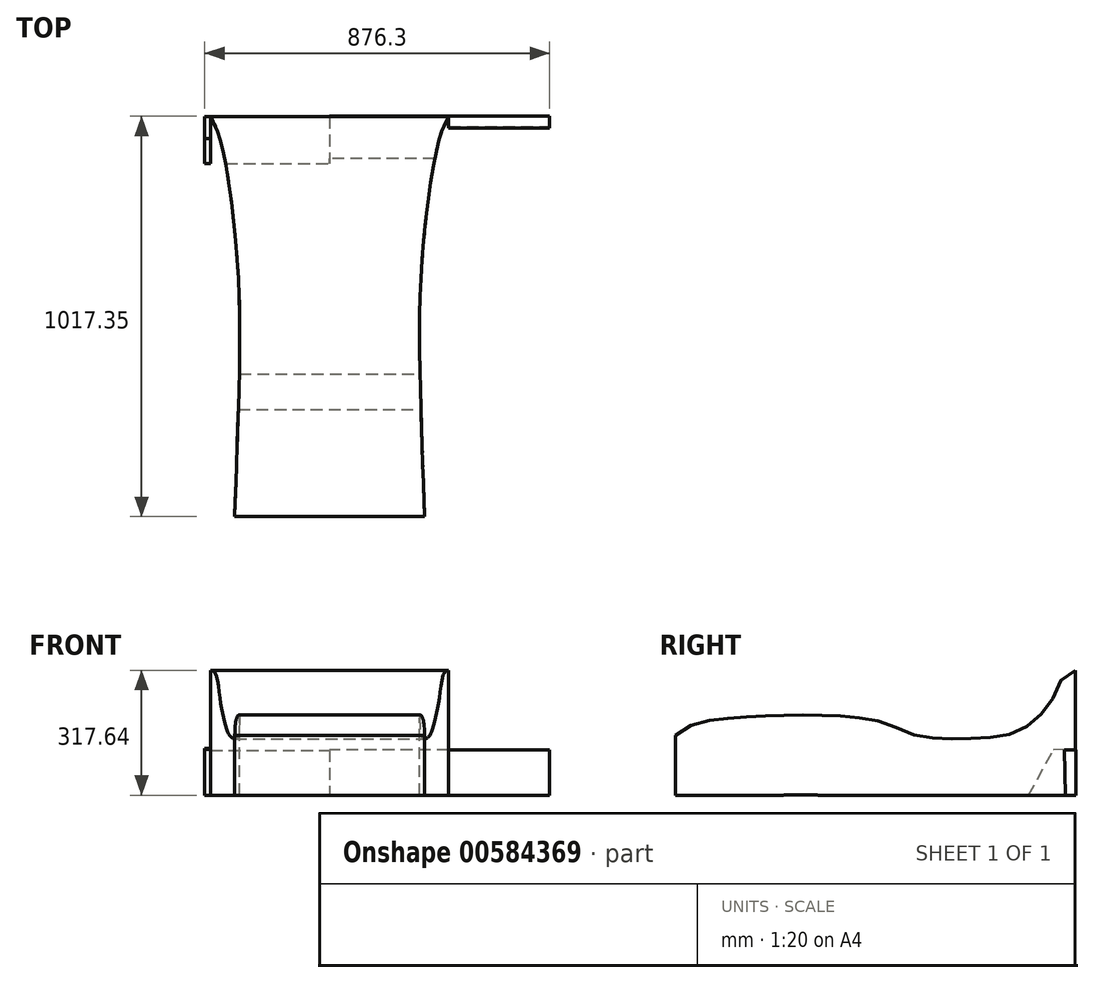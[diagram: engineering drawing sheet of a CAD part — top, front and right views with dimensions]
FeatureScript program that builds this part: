
annotation { "Feature Type Name" : "Feature", "Feature Type Description" : "" }
export const myFeature = defineFeature(function(context is Context, id is Id, definition is map)
    precondition{}
    {
        {
            var Q0;
            Q0=qCreatedBy(makeId("Front.planeOp"),FACE);
            var sketch = newSketch(context, id + "F0", { "sketchPlane" : qUnion([Q0])});
            skLineSegment(sketch, "E0", {"start": v(0, 0) * mm, "end": v(241.3, 0) * mm});
            skLineSegment(sketch, "E1", {"start": v(241.3, 0) * mm, "end": v(241.3, -38.1) * mm});
            skLineSegment(sketch, "E2", {"start": v(241.3, -38.1) * mm, "end": v(0, -38.1) * mm});
            skLineSegment(sketch, "E3", {"start": v(0, -38.1) * mm, "end": v(-241.3, -38.1) * mm});
            skLineSegment(sketch, "E4", {"start": v(-241.3, -38.1) * mm, "end": v(-241.3, 0) * mm});
            skLineSegment(sketch, "E5", {"start": v(-241.3, 0) * mm, "end": v(0, 0) * mm});
            skSolve(sketch);
        }
        {
            var Q0;
            Q0=qCreatedBy(makeId("Right.planeOp"),FACE);
            var sketch = newSketch(context, id + "F1", { "sketchPlane" : qUnion([Q0])});
            skFitSpline(sketch, "E6", {"points": [v(0, 0) * mm, v(24.74, 16.6) * mm, v(49, 28.94) * mm, v(187.46, 47.43) * mm, v(521.37, 34.71) * mm, v(607.94, 0) * mm, v(838.07, 0) * mm, v(901.63, 29.24) * mm, v(960.8, 98.27) * mm, v(1016, 165.1) * mm], "startDerivative": vector(273.3, 180.11) * mm, "endDerivative": vector(1078.66, 86.3) * mm});
            skLineSegment(sketch, "E7.0", {"start": v(0, -38.1) * mm, "end": v(0, 0) * mm, "construction": true});
            skLineSegment(sketch, "E8", {"start": v(0, -38.1) * mm, "end": v(1016, -38.1) * mm});
            skLineSegment(sketch, "E9", {"start": v(1016, 165.1) * mm, "end": v(1016, -38.1) * mm, "construction": true});
            skSolve(sketch);
        }
        {
            var Q0;
            Q0=qCreatedBy(makeId("Front.planeOp"),FACE);
            cPlane(context, id + "F2", {"entities" : qUnion([Q0]), "cplaneType" : CPlaneType.OFFSET, "offset" : 1016 * mm, "oppositeDirection" : true, "width" : 152.4 * mm, "height" : 152.4 * mm});
        }
        {
            var Q0;
            Q0=qCreatedBy(id+"F2.planeOp",FACE);
            var sketch = newSketch(context, id + "F3", { "sketchPlane" : qUnion([Q0])});
            skPoint(sketch, "E10.0", {"position": v(0, 165.1) * mm});
            skPoint(sketch, "E11.0", {"position": v(0, -38.1) * mm});
            skLineSegment(sketch, "E12", {"start": v(0, 165.1) * mm, "end": v(302.62, 165.1) * mm});
            skLineSegment(sketch, "E13", {"start": v(302.62, 165.1) * mm, "end": v(302.62, -38.1) * mm});
            skLineSegment(sketch, "E14", {"start": v(302.62, -38.1) * mm, "end": v(0, -38.1) * mm});
            skLineSegment(sketch, "E15", {"start": v(0, 165.1) * mm, "end": v(0, -38.1) * mm, "construction": true});
            skLineSegment(sketch, "E16.MirrorCS", {"start": v(0, 165.1) * mm, "end": v(-302.62, 165.1) * mm});
            skLineSegment(sketch, "E17.MirrorCS", {"start": v(-302.62, 165.1) * mm, "end": v(-302.62, -38.1) * mm});
            skLineSegment(sketch, "E18.MirrorCS", {"start": v(-302.62, -38.1) * mm, "end": v(0, -38.1) * mm});
            skSolve(sketch);
        }
        {
            var Q0;
            Q0=makeQuery(id+"F3.imprint","IMPRINT",FACE,{"disambiguationData":[TD([[makeQuery(id+"F3.imprint","IMPRINT",EDGE,{"derivedFrom":sQuery(id+"F3.wireOp",EDGE,"E12")}),-1.0]])]});
            var Q1;
            Q1=sQuery(id+"F1.wireOp",EDGE,"E6");
            sweep(context, id + "F4", {"profiles" : qUnion([Q0]), "path" : qUnion([Q1]), "keepProfileOrientation" : true});
        }
        {
            var Q0;
            Q0=qCreatedBy(makeId("Right.planeOp"),FACE);
            var sketch = newSketch(context, id + "F5", { "sketchPlane" : qUnion([Q0])});
            skLineSegment(sketch, "E19", {"start": v(0, -254) * mm, "end": v(1016, -254) * mm});
            skLineSegment(sketch, "E20", {"start": v(0, -254) * mm, "end": v(0, 0) * mm, "construction": true});
            skLineSegment(sketch, "E21", {"start": v(0, 0) * mm, "end": v(4.95, -3.69) * mm});
            skLineSegment(sketch, "E22", {"start": v(0, -254) * mm, "end": v(0, -152.4) * mm});
            skLineSegment(sketch, "E23", {"start": v(0, -152.4) * mm, "end": v(1016, -152.4) * mm});
            skLineSegment(sketch, "E24", {"start": v(1016, -152.4) * mm, "end": v(1016, -254) * mm});
            skPoint(sketch, "E25.0", {"position": v(1016, 165.1) * mm});
            skLineSegment(sketch, "E26.0", {"start": v(1016, 165.1) * mm, "end": v(1016, -38.1) * mm, "construction": true});
            skFitSpline(sketch, "E27.0.0", {"points": [v(1016, 165.1) * mm, v(993.53, 163.3) * mm, v(983.17, 149.03) * mm, v(971.07, 122.78) * mm, v(967.6, 113.22) * mm, v(961.43, 99.41) * mm, v(959.18, 94.92) * mm, v(954.24, 86.25) * mm, v(951.57, 82.07) * mm, v(937.48, 61.91) * mm, v(923.82, 48.21) * mm, v(907.79, 34.29) * mm, v(904.63, 31.66) * mm, v(898.53, 26.74) * mm, v(895.58, 24.44) * mm, v(886.71, 17.98) * mm, v(880.77, 14.27) * mm, v(867.07, 7.78) * mm, v(859.32, 5.02) * mm, v(845.03, 1.4) * mm, v(839.81, 0.29) * mm, v(828.32, -1.8) * mm, v(822.06, -2.75) * mm, v(788.79, -7.11) * mm, v(755.73, -9.2) * mm, v(689.68, -9.71) * mm, v(656.7, -8.12) * mm, v(623.6, -3.25) * mm, v(617.4, -2.14) * mm, v(605.99, 0.4) * mm, v(600.83, 1.82) * mm, v(586.6, 6.46) * mm, v(578.72, 10.03) * mm, v(556.08, 21.2) * mm, v(542.27, 29.24) * mm, v(496.51, 41.25) * mm, v(464.99, 45.3) * mm, v(357.79, 52.9) * mm, v(269.5, 51.86) * mm, v(182.6, 47.21) * mm, v(166.46, 46.12) * mm, v(136.89, 43.66) * mm, v(123.42, 42.3) * mm, v(87.08, 37.85) * mm, v(68.23, 34.42) * mm, v(51.62, 29.8) * mm, v(48.66, 28.87) * mm, v(43.37, 26.95) * mm, v(41.02, 25.96) * mm, v(34.44, 22.81) * mm, v(30.65, 20.48) * mm, v(24.13, 16.21) * mm, v(21.78, 14.64) * mm, v(16.93, 11.4) * mm, v(14.44, 9.72) * mm, v(7.26, 4.87) * mm, v(2.85, 1.88) * mm, v(0, 0) * mm], "construction": true});
            skLineSegment(sketch, "E27.0.1", {"start": v(0, -203.2) * mm, "end": v(0, 0) * mm, "construction": true});
            skFitSpline(sketch, "E27.0.2", {"points": [v(0, -203.2) * mm, v(2.85, -201.32) * mm, v(7.26, -198.33) * mm, v(14.44, -193.48) * mm, v(16.93, -191.8) * mm, v(21.78, -188.56) * mm, v(24.13, -186.99) * mm, v(30.65, -182.72) * mm, v(34.44, -180.39) * mm, v(41.02, -177.24) * mm, v(43.37, -176.25) * mm, v(48.66, -174.33) * mm, v(51.62, -173.4) * mm, v(68.23, -168.78) * mm, v(87.08, -165.35) * mm, v(123.42, -160.9) * mm, v(136.89, -159.54) * mm, v(166.46, -157.08) * mm, v(182.6, -155.99) * mm, v(269.5, -151.34) * mm, v(357.79, -150.3) * mm, v(464.99, -157.9) * mm, v(496.51, -161.95) * mm, v(542.27, -173.96) * mm, v(556.08, -182) * mm, v(578.72, -193.17) * mm, v(586.6, -196.74) * mm, v(600.83, -201.38) * mm, v(605.99, -202.8) * mm, v(617.4, -205.34) * mm, v(623.6, -206.45) * mm, v(656.7, -211.32) * mm, v(689.68, -212.91) * mm, v(755.73, -212.4) * mm, v(788.79, -210.31) * mm, v(822.06, -205.95) * mm, v(828.32, -205) * mm, v(839.81, -202.91) * mm, v(845.03, -201.8) * mm, v(859.32, -198.18) * mm, v(867.07, -195.42) * mm, v(880.77, -188.93) * mm, v(886.71, -185.22) * mm, v(895.58, -178.76) * mm, v(898.53, -176.46) * mm, v(904.63, -171.54) * mm, v(907.79, -168.91) * mm, v(923.82, -154.99) * mm, v(937.48, -141.29) * mm, v(951.57, -121.13) * mm, v(954.24, -116.95) * mm, v(959.18, -108.28) * mm, v(961.43, -103.79) * mm, v(967.6, -89.98) * mm, v(971.07, -80.42) * mm, v(983.17, -54.17) * mm, v(993.53, -39.9) * mm, v(1016, -38.1) * mm], "construction": true});
            skLineSegment(sketch, "E27.0.3", {"start": v(1016, -38.1) * mm, "end": v(1016, 165.1) * mm, "construction": true});
            skLineSegment(sketch, "E28", {"start": v(1016, -152.4) * mm, "end": v(1016, 165.1) * mm, "construction": true});
            skLineSegment(sketch, "E29", {"start": v(0, -152.4) * mm, "end": v(0, -254) * mm});
            skLineSegment(sketch, "E30", {"start": v(1016, -254) * mm, "end": v(1016, -152.4) * mm});
            skSolve(sketch);
        }
        {
            var Q0;
            Q0=makeQuery(id+"F5.imprint","IMPRINT",FACE,{"disambiguationData":[TD([[makeQuery(id+"F5.imprint","IMPRINT",EDGE,{"derivedFrom":sQuery(id+"F5.wireOp",EDGE,"E19")}),1.0]])]});
            extrude(context, id + "F6", {"entities" : qUnion([Q0]), "operationType" : NewBodyOperationType.REMOVE, "endBound" : BoundingType.SYMMETRIC, "oppositeDirection" : true, "depth" : 1016 * mm, "offsetDistance" : 25.4 * mm});
        }
        {
            var Q0;
            Q0=qCreatedBy(makeId("Top.planeOp"),FACE);
            var sketch = newSketch(context, id + "F7", { "sketchPlane" : qUnion([Q0])});
            skPoint(sketch, "E31.0", {"position": v(-302.62, 1016) * mm});
            skPoint(sketch, "E32.0", {"position": v(-302.62, 0) * mm});
            skPoint(sketch, "E33.0", {"position": v(302.62, 0) * mm});
            skPoint(sketch, "E34.0", {"position": v(302.62, 1016) * mm});
            skLineSegment(sketch, "E35", {"start": v(302.62, 1016) * mm, "end": v(-302.62, 1016) * mm});
            skPoint(sketch, "E36.0", {"position": v(-241.3, 0) * mm});
            skPoint(sketch, "E37.0", {"position": v(241.3, 0) * mm});
            skLineSegment(sketch, "E38", {"start": v(0, 0) * mm, "end": v(-241.3, 0) * mm});
            skLineSegment(sketch, "E39", {"start": v(0, 0) * mm, "end": v(241.3, 0) * mm});
            skFitSpline(sketch, "E40", {"points": [v(-241.3, 0) * mm, v(-228.4, 486.07) * mm, v(-240.54, 716.58) * mm, v(-268.2, 915.96) * mm, v(-302.62, 1016) * mm], "startDerivative": vector(44.02, 1254.78) * mm, "endDerivative": vector(-240.1, 317.97) * mm});
            skLineSegment(sketch, "E41.MirrorCS", {"start": v(302.62, 1016) * mm, "end": v(302.62, 1016) * mm});
            skLineSegment(sketch, "E42", {"start": v(-302.62, 1016) * mm, "end": v(-302.62, 0) * mm});
            skLineSegment(sketch, "E43", {"start": v(-241.3, 0) * mm, "end": v(-302.62, 0) * mm});
            skLineSegment(sketch, "E44", {"start": v(241.3, 0) * mm, "end": v(302.62, 0) * mm});
            skFitSpline(sketch, "E45.MirrorCS", {"points": [v(241.3, 0) * mm, v(228.4, 486.07) * mm, v(240.54, 716.58) * mm, v(268.2, 915.96) * mm, v(302.62, 1016) * mm], "startDerivative": vector(-44.02, 1254.78) * mm, "endDerivative": vector(240.1, 317.97) * mm});
            skLineSegment(sketch, "E46", {"start": v(241.3, 0) * mm, "end": v(0, 0) * mm});
            skLineSegment(sketch, "E47", {"start": v(302.62, 1016) * mm, "end": v(302.62, 0) * mm});
            skSolve(sketch);
        }
        {
            var Q0;
            Q0=makeQuery(id+"F5.imprint","IMPRINT",FACE,{"disambiguationData":[TD([[makeQuery(id+"F5.imprint","IMPRINT",EDGE,{"derivedFrom":sQuery(id+"F5.wireOp",EDGE,"E19")}),1.0]])]});
            var sketch = newSketch(context, id + "F8", { "sketchPlane" : qUnion([Q0])});
            skLineSegment(sketch, "E48", {"start": v(1017.35, -37.09) * mm, "end": v(1017.35, -152.54) * mm});
            skLineSegment(sketch, "E49", {"start": v(1017.35, -152.54) * mm, "end": v(909.64, -152.54) * mm});
            skLineSegment(sketch, "E50", {"start": v(909.64, -152.54) * mm, "end": v(987.9, -37.86) * mm});
            skLineSegment(sketch, "E51", {"start": v(987.9, -37.86) * mm, "end": v(1017.35, -37.09) * mm});
            skSolve(sketch);
        }
        {
            var Q0;
            Q0 = qSketchRegion(id + "F8", true);
            extrude(context, id + "F9", {"entities" : qUnion([Q0]), "operationType" : NewBodyOperationType.ADD, "depth" : 558.8 * mm, "offsetDistance" : 25.4 * mm});
        }
        {
            var Q0;
            Q0=makeQuery(id+"F9.opExtrude","CAP_FACE",FACE,{"disambiguationData":[OSD([sQuery(id+"F8.wireOp",EDGE,"E48"),sQuery(id+"F8.wireOp",EDGE,"E49"),sQuery(id+"F8.wireOp",EDGE,"E50"),sQuery(id+"F8.wireOp",EDGE,"E51")])],"isStart":true});
            var sketch = newSketch(context, id + "F10", { "sketchPlane" : qUnion([Q0])});
            skLineSegment(sketch, "E52", {"start": v(-1016, -38.1) * mm, "end": v(-1017.35, -152.54) * mm});
            skLineSegment(sketch, "E53", {"start": v(-1017.35, -152.54) * mm, "end": v(-917.73, -152.4) * mm});
            skLineSegment(sketch, "E54", {"start": v(-917.73, -152.4) * mm, "end": v(-976.8, -38.1) * mm});
            skLineSegment(sketch, "E55", {"start": v(-976.8, -38.1) * mm, "end": v(-1016, -37.12) * mm});
            skSolve(sketch);
        }
        {
            var Q0;
            Q0=makeQuery(id+"F10.imprint","IMPRINT",FACE,{"disambiguationData":[TD([[makeQuery(id+"F10.imprint","IMPRINT",EDGE,{"derivedFrom":sQuery(id+"F10.wireOp",EDGE,"E52")}),1.0]])]});
            var sketch = newSketch(context, id + "F11", { "sketchPlane" : qUnion([Q0])});
            skLineSegment(sketch, "E56", {"start": v(-1015.98, -34.01) * mm, "end": v(-1015.98, -152.44) * mm});
            skLineSegment(sketch, "E57", {"start": v(-1015.98, -152.44) * mm, "end": v(-896.78, -152.44) * mm});
            skLineSegment(sketch, "E58", {"start": v(-896.78, -152.44) * mm, "end": v(-960.4, -36.7) * mm});
            skLineSegment(sketch, "E59", {"start": v(-960.4, -36.7) * mm, "end": v(-1015.98, -34.01) * mm});
            skSolve(sketch);
        }
        {
            var Q0;
            Q0 = qSketchRegion(id + "F11", true);
            extrude(context, id + "F12", {"entities" : qUnion([Q0]), "operationType" : NewBodyOperationType.ADD, "depth" : 317.5 * mm, "offsetDistance" : 25.4 * mm});
        }
        {
            var Q0;
            Q0=makeQuery(id+"F7.imprint","IMPRINT",FACE,{"disambiguationData":[TD([[makeQuery(id+"F7.imprint","IMPRINT",EDGE,{"derivedFrom":sQuery(id+"F7.wireOp",EDGE,"E40")}),1.0]])]});
            var Q1;
            Q1=makeQuery(id+"F7.imprint","IMPRINT",FACE,{"disambiguationData":[TD([[makeQuery(id+"F7.imprint","IMPRINT",EDGE,{"derivedFrom":sQuery(id+"F7.wireOp",EDGE,"E45.MirrorCS")}),-1.0]])]});
            extrude(context, id + "F13", {"entities" : qUnion([Q0, Q1]), "operationType" : NewBodyOperationType.REMOVE, "endBound" : BoundingType.SYMMETRIC, "oppositeDirection" : true, "depth" : 508 * mm, "offsetDistance" : 25.4 * mm});
        }
        {
            var Q0;
            Q0=makeQuery(id+"F9.opExtrude","SWEPT_FACE",FACE,{"disambiguationData":[OSD([sQuery(id+"F8.wireOp",EDGE,"E51")])]});
            var sketch = newSketch(context, id + "F14", { "sketchPlane" : qUnion([Q0])});
            skLineSegment(sketch, "E60.bottom", {"start": v(302.62, 1014.67) * mm, "end": v(628.68, 1014.67) * mm});
            skLineSegment(sketch, "E60.top", {"start": v(302.62, 871.04) * mm, "end": v(628.68, 871.04) * mm});
            skLineSegment(sketch, "E60.left", {"start": v(302.62, 1014.67) * mm, "end": v(302.62, 871.04) * mm});
            skLineSegment(sketch, "E60.right", {"start": v(628.68, 1014.67) * mm, "end": v(628.68, 871.04) * mm});
            skSolve(sketch);
        }
        {
            var Q0;
            {var subQ4=sQuery(id+"F14.wireOp",EDGE,"E60.top");Q0=makeQuery(id+"F14.imprint","IMPRINT",FACE,{"disambiguationData":[TD([[makeQuery(id+"F14.imprint","IMPRINT",EDGE,{"derivedFrom":subQ4}),1.0]])]});}
            extrude(context, id + "F15", {"entities" : qUnion([Q0]), "operationType" : NewBodyOperationType.REMOVE, "oppositeDirection" : true, "depth" : 254 * mm, "offsetDistance" : 25.4 * mm});
        }
    });
